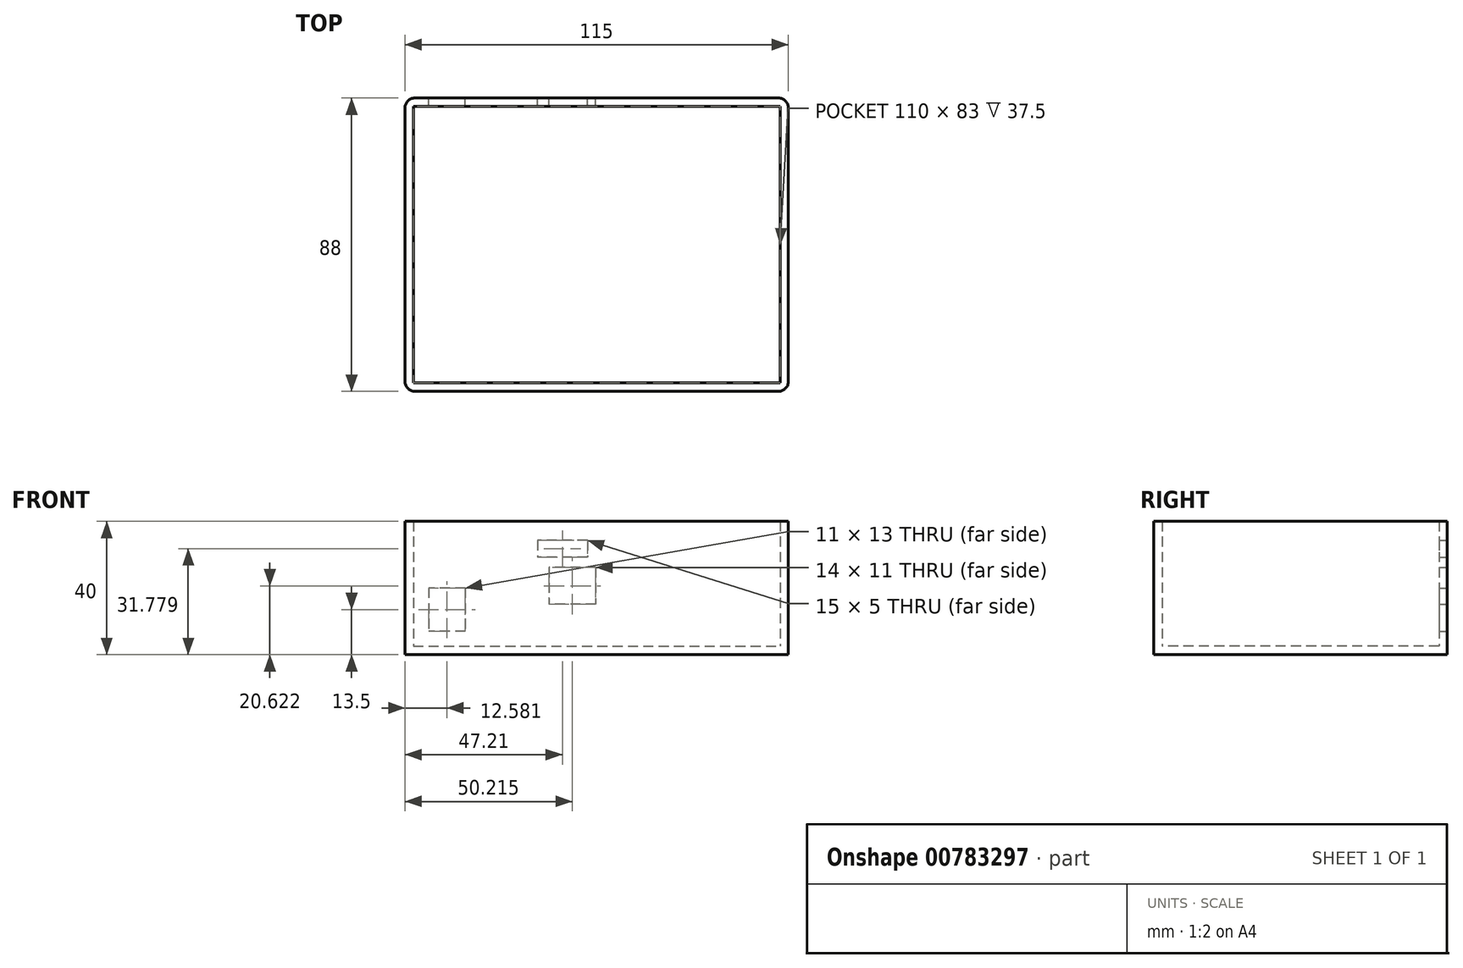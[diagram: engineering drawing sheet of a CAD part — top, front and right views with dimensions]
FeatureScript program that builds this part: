
annotation { "Feature Type Name" : "Feature", "Feature Type Description" : "" }
export const myFeature = defineFeature(function(context is Context, id is Id, definition is map)
    precondition{}
    {
        {
            var Q0;
            Q0=qCreatedBy(makeId("Top.planeOp"),FACE);
            var sketch = newSketch(context, id + "F0", { "sketchPlane" : qUnion([Q0])});
            skLineSegment(sketch, "E0.bottom", {"start": v(-55.09, 41.87) * mm, "end": v(59.91, 41.87) * mm});
            skLineSegment(sketch, "E0.top", {"start": v(-55.09, -46.13) * mm, "end": v(59.91, -46.13) * mm});
            skLineSegment(sketch, "E0.left", {"start": v(-55.09, 41.87) * mm, "end": v(-55.09, -46.13) * mm});
            skLineSegment(sketch, "E0.right", {"start": v(59.91, 41.87) * mm, "end": v(59.91, -46.13) * mm});
            skSolve(sketch);
        }
        {
            var Q0;
            Q0 = qSketchRegion(id + "F0", true);
            extrude(context, id + "F1", {"entities" : qUnion([Q0]), "depth" : 40 * mm, "offsetDistance" : 25 * mm});
        }
        {
            var Q0;
            Q0=makeQuery(id+"F1.opExtrude","CAP_FACE",FACE,{"disambiguationData":[OSD([sQuery(id+"F0.wireOp",EDGE,"E0.bottom"),sQuery(id+"F0.wireOp",EDGE,"E0.top"),sQuery(id+"F0.wireOp",EDGE,"E0.left"),sQuery(id+"F0.wireOp",EDGE,"E0.right")])],"isStart":false});
            shell(context, id + "F2", {"entities" : qUnion([Q0]), "thickness" : 2.5 * mm});
        }
        {
            var Q0;
            Q0=makeQuery(id+"F1.opExtrude","SWEPT_FACE",FACE,{"disambiguationData":[OSD([sQuery(id+"F0.wireOp",EDGE,"E0.bottom")])]});
            var sketch = newSketch(context, id + "F3", { "sketchPlane" : qUnion([Q0])});
            skLineSegment(sketch, "E1.bottom", {"start": v(0.38, 34.28) * mm, "end": v(15.38, 34.28) * mm});
            skLineSegment(sketch, "E1.top", {"start": v(0.38, 29.28) * mm, "end": v(15.38, 29.28) * mm});
            skLineSegment(sketch, "E1.left", {"start": v(0.38, 34.28) * mm, "end": v(0.38, 29.28) * mm});
            skLineSegment(sketch, "E1.right", {"start": v(15.38, 34.28) * mm, "end": v(15.38, 29.28) * mm});
            skLineSegment(sketch, "E2.bottom", {"start": v(-2.13, 26.12) * mm, "end": v(11.87, 26.12) * mm});
            skLineSegment(sketch, "E2.top", {"start": v(-2.13, 15.12) * mm, "end": v(11.87, 15.12) * mm});
            skLineSegment(sketch, "E2.left", {"start": v(-2.13, 26.12) * mm, "end": v(-2.13, 15.12) * mm});
            skLineSegment(sketch, "E2.right", {"start": v(11.87, 26.12) * mm, "end": v(11.87, 15.12) * mm});
            skLineSegment(sketch, "E3.bottom", {"start": v(37, 20) * mm, "end": v(48, 20) * mm});
            skLineSegment(sketch, "E3.top", {"start": v(37, 7) * mm, "end": v(48, 7) * mm});
            skLineSegment(sketch, "E3.left", {"start": v(37, 20) * mm, "end": v(37, 7) * mm});
            skLineSegment(sketch, "E3.right", {"start": v(48, 20) * mm, "end": v(48, 7) * mm});
            skLineSegment(sketch, "E4", {"start": v(48, 7) * mm, "end": v(55, 7) * mm});
            skLineSegment(sketch, "E5", {"start": v(52.22, 7) * mm, "end": v(52.22, 0) * mm});
            skSolve(sketch);
        }
        {
            var Q0;
            Q0 = qSketchRegion(id + "F3", true);
            extrude(context, id + "F4", {"entities" : qUnion([Q0]), "operationType" : NewBodyOperationType.REMOVE, "oppositeDirection" : true, "depth" : 2.5 * mm, "offsetDistance" : 25 * mm});
        }
        {
            var Q0;
            Q0=makeQuery(id+"F1.opExtrude","SWEPT_EDGE",EDGE,{"disambiguationData":[OSD([sQuery(id+"F0.wireOp",EDGE,"E0.top"),sQuery(id+"F0.wireOp",EDGE,"E0.right")])]});
            var Q1;
            Q1=makeQuery(id+"F1.opExtrude","SWEPT_EDGE",EDGE,{"disambiguationData":[OSD([sQuery(id+"F0.wireOp",EDGE,"E0.top"),sQuery(id+"F0.wireOp",EDGE,"E0.left")])]});
            var Q2;
            Q2=makeQuery(id+"F1.opExtrude","SWEPT_EDGE",EDGE,{"disambiguationData":[OSD([sQuery(id+"F0.wireOp",EDGE,"E0.bottom"),sQuery(id+"F0.wireOp",EDGE,"E0.left")])]});
            var Q3;
            Q3=makeQuery(id+"F1.opExtrude","SWEPT_EDGE",EDGE,{"disambiguationData":[OSD([sQuery(id+"F0.wireOp",EDGE,"E0.bottom"),sQuery(id+"F0.wireOp",EDGE,"E0.right")])]});
            fillet(context, id + "F5", {"entities" : qUnion([Q0, Q1, Q2, Q3]), "radius" : 3 * mm, "tangentPropagation" : true, "allowEdgeOverflow" : false});
        }
    });
